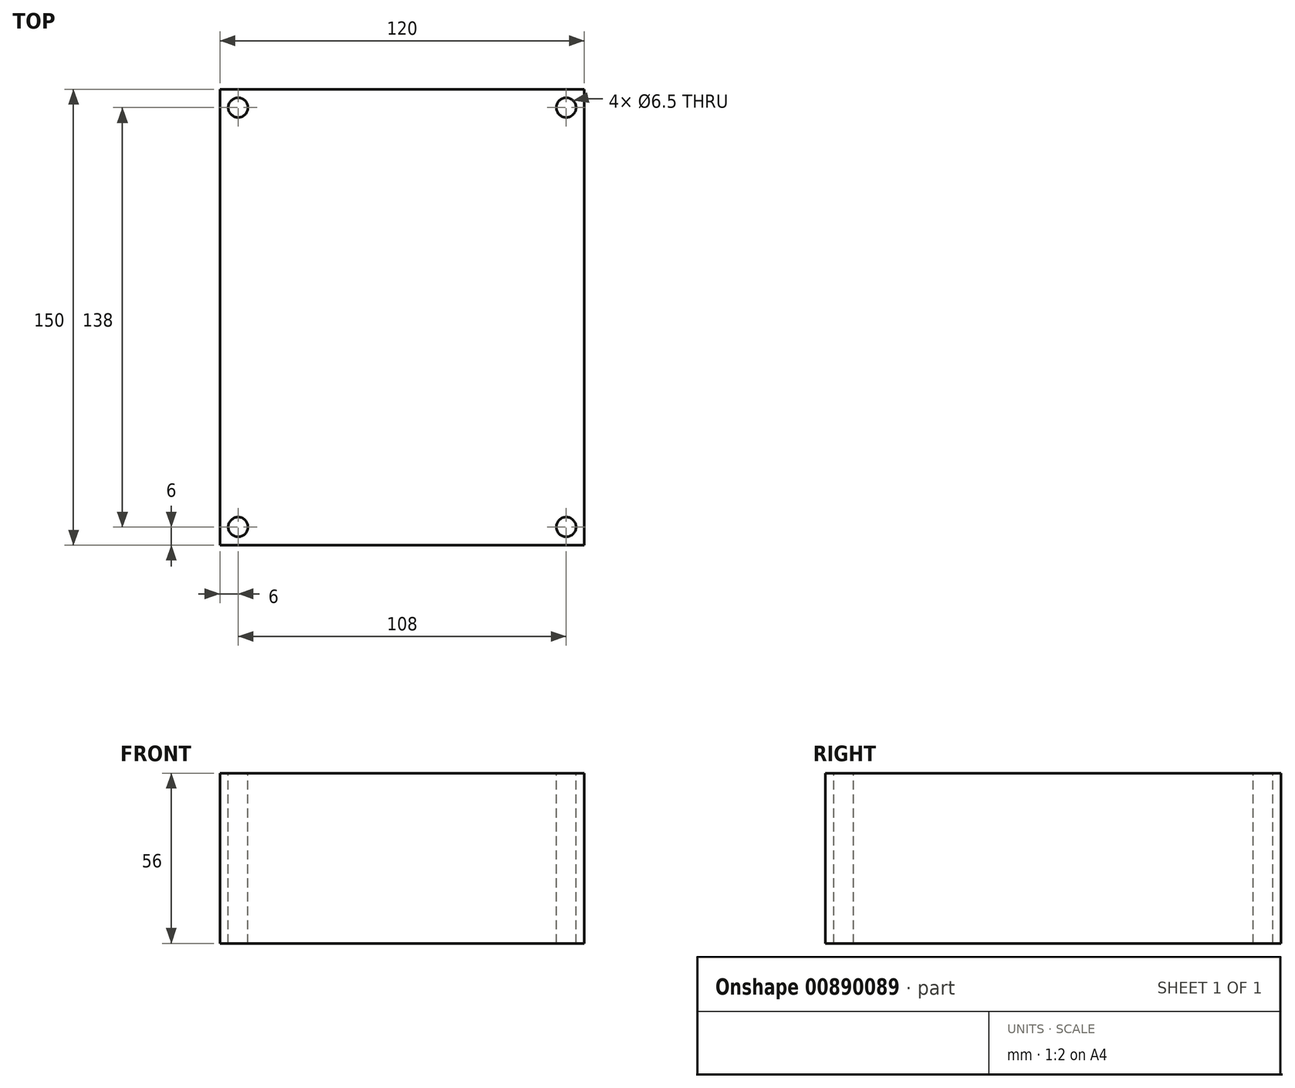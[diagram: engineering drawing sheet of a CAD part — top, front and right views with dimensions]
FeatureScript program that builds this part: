
annotation { "Feature Type Name" : "Feature", "Feature Type Description" : "" }
export const myFeature = defineFeature(function(context is Context, id is Id, definition is map)
    precondition{}
    {
        {
            var Q0;
            Q0=qCreatedBy(makeId("Top.planeOp"),FACE);
            var sketch = newSketch(context, id + "F0", { "sketchPlane" : qUnion([Q0])});
            skLineSegment(sketch, "E0.bottom", {"start": v(-60, 75) * mm, "end": v(60, 75) * mm});
            skLineSegment(sketch, "E0.top", {"start": v(-60, -75) * mm, "end": v(60, -75) * mm});
            skLineSegment(sketch, "E0.left", {"start": v(-60, 75) * mm, "end": v(-60, -75) * mm});
            skLineSegment(sketch, "E0.right", {"start": v(60, 75) * mm, "end": v(60, -75) * mm});
            skPoint(sketch, "E0.middle", {"position": v(0, 0) * mm});
            skSolve(sketch);
        }
        {
            var Q0;
            Q0 = qSketchRegion(id + "F0", true);
            extrude(context, id + "F1", {"entities" : qUnion([Q0]), "depth" : 56 * mm, "offsetDistance" : 25 * mm});
        }
        {
            var Q0;
            Q0=makeQuery(id+"F1.opExtrude","CAP_FACE",FACE,{"disambiguationData":[OSD([sQuery(id+"F0.wireOp",EDGE,"E0.bottom"),sQuery(id+"F0.wireOp",EDGE,"E0.top"),sQuery(id+"F0.wireOp",EDGE,"E0.left"),sQuery(id+"F0.wireOp",EDGE,"E0.right")])],"isStart":false});
            var sketch = newSketch(context, id + "F2", { "sketchPlane" : qUnion([Q0])});
            skLineSegment(sketch, "E1.bottom", {"start": v(-54, 69) * mm, "end": v(54, 69) * mm});
            skLineSegment(sketch, "E1.top", {"start": v(-54, -69) * mm, "end": v(54, -69) * mm});
            skLineSegment(sketch, "E1.left", {"start": v(-54, 69) * mm, "end": v(-54, -69) * mm});
            skLineSegment(sketch, "E1.right", {"start": v(54, 69) * mm, "end": v(54, -69) * mm});
            skPoint(sketch, "E1.middle", {"position": v(0, 0) * mm});
            skCircle(sketch, "E2", {"center": v(-54, 69) * mm, "radius": 3.25 * mm});
            skCircle(sketch, "E3.MirrorC", {"center": v(54, 69) * mm, "radius": 3.25 * mm});
            skCircle(sketch, "E4.MirrorC", {"center": v(-54, -69) * mm, "radius": 3.25 * mm});
            skCircle(sketch, "E5.MirrorC", {"center": v(54, -69) * mm, "radius": 3.25 * mm});
            skSolve(sketch);
        }
        {
            var Q0;
            {var subQ0=sQuery(id+"F2.wireOp",EDGE,"E1.left");var subQ1=sQuery(id+"F2.wireOp",EDGE,"E1.bottom");var subQ2=makeQuery(id+"F2.imprint","INTERSECT",VERTEX,{"derivedFrom":[subQ1,subQ0]});Q0=makeQuery(id+"F2.imprint","IMPRINT",FACE,{"disambiguationData":[TD([[makeQuery(id+"F2.imprint","IMPRINT",EDGE,{"disambiguationData":[TD([[subQ2,-1.0]])],"derivedFrom":subQ1}),1.0]])]});}
            var Q1;
            {var subQ0=sQuery(id+"F2.wireOp",EDGE,"E1.left");var subQ1=sQuery(id+"F2.wireOp",EDGE,"E1.bottom");var subQ2=makeQuery(id+"F2.imprint","INTERSECT",VERTEX,{"derivedFrom":[subQ1,subQ0]});Q1=makeQuery(id+"F2.imprint","IMPRINT",FACE,{"disambiguationData":[TD([[makeQuery(id+"F2.imprint","IMPRINT",EDGE,{"disambiguationData":[TD([[subQ2,-1.0]])],"derivedFrom":subQ1}),-1.0]])]});}
            var Q2;
            {var subQ0=sQuery(id+"F2.wireOp",EDGE,"E1.right");var subQ1=sQuery(id+"F2.wireOp",EDGE,"E1.bottom");var subQ2=makeQuery(id+"F2.imprint","INTERSECT",VERTEX,{"derivedFrom":[subQ1,subQ0]});Q2=makeQuery(id+"F2.imprint","IMPRINT",FACE,{"disambiguationData":[TD([[makeQuery(id+"F2.imprint","IMPRINT",EDGE,{"disambiguationData":[TD([[subQ2,1.0]])],"derivedFrom":subQ1}),1.0]])]});}
            var Q3;
            {var subQ0=sQuery(id+"F2.wireOp",EDGE,"E1.right");var subQ1=sQuery(id+"F2.wireOp",EDGE,"E1.bottom");var subQ2=makeQuery(id+"F2.imprint","INTERSECT",VERTEX,{"derivedFrom":[subQ1,subQ0]});Q3=makeQuery(id+"F2.imprint","IMPRINT",FACE,{"disambiguationData":[TD([[makeQuery(id+"F2.imprint","IMPRINT",EDGE,{"disambiguationData":[TD([[subQ2,1.0]])],"derivedFrom":subQ1}),-1.0]])]});}
            var Q4;
            {var subQ0=sQuery(id+"F2.wireOp",EDGE,"E1.left");var subQ1=sQuery(id+"F2.wireOp",EDGE,"E1.top");var subQ2=makeQuery(id+"F2.imprint","INTERSECT",VERTEX,{"derivedFrom":[subQ1,subQ0]});Q4=makeQuery(id+"F2.imprint","IMPRINT",FACE,{"disambiguationData":[TD([[makeQuery(id+"F2.imprint","IMPRINT",EDGE,{"disambiguationData":[TD([[subQ2,-1.0]])],"derivedFrom":subQ1}),-1.0]])]});}
            var Q5;
            {var subQ0=sQuery(id+"F2.wireOp",EDGE,"E1.left");var subQ1=sQuery(id+"F2.wireOp",EDGE,"E1.top");var subQ2=makeQuery(id+"F2.imprint","INTERSECT",VERTEX,{"derivedFrom":[subQ1,subQ0]});Q5=makeQuery(id+"F2.imprint","IMPRINT",FACE,{"disambiguationData":[TD([[makeQuery(id+"F2.imprint","IMPRINT",EDGE,{"disambiguationData":[TD([[subQ2,-1.0]])],"derivedFrom":subQ1}),1.0]])]});}
            var Q6;
            {var subQ0=sQuery(id+"F2.wireOp",EDGE,"E1.right");var subQ1=sQuery(id+"F2.wireOp",EDGE,"E1.top");var subQ2=makeQuery(id+"F2.imprint","INTERSECT",VERTEX,{"derivedFrom":[subQ1,subQ0]});Q6=makeQuery(id+"F2.imprint","IMPRINT",FACE,{"disambiguationData":[TD([[makeQuery(id+"F2.imprint","IMPRINT",EDGE,{"disambiguationData":[TD([[subQ2,1.0]])],"derivedFrom":subQ1}),-1.0]])]});}
            var Q7;
            {var subQ0=sQuery(id+"F2.wireOp",EDGE,"E1.right");var subQ1=sQuery(id+"F2.wireOp",EDGE,"E1.top");var subQ2=makeQuery(id+"F2.imprint","INTERSECT",VERTEX,{"derivedFrom":[subQ1,subQ0]});Q7=makeQuery(id+"F2.imprint","IMPRINT",FACE,{"disambiguationData":[TD([[makeQuery(id+"F2.imprint","IMPRINT",EDGE,{"disambiguationData":[TD([[subQ2,1.0]])],"derivedFrom":subQ1}),1.0]])]});}
            extrude(context, id + "F3", {"entities" : qUnion([Q0, Q1, Q2, Q3, Q4, Q5, Q6, Q7]), "operationType" : NewBodyOperationType.REMOVE, "oppositeDirection" : true, "depth" : 67.5 * mm, "offsetDistance" : 25 * mm});
        }
    });
